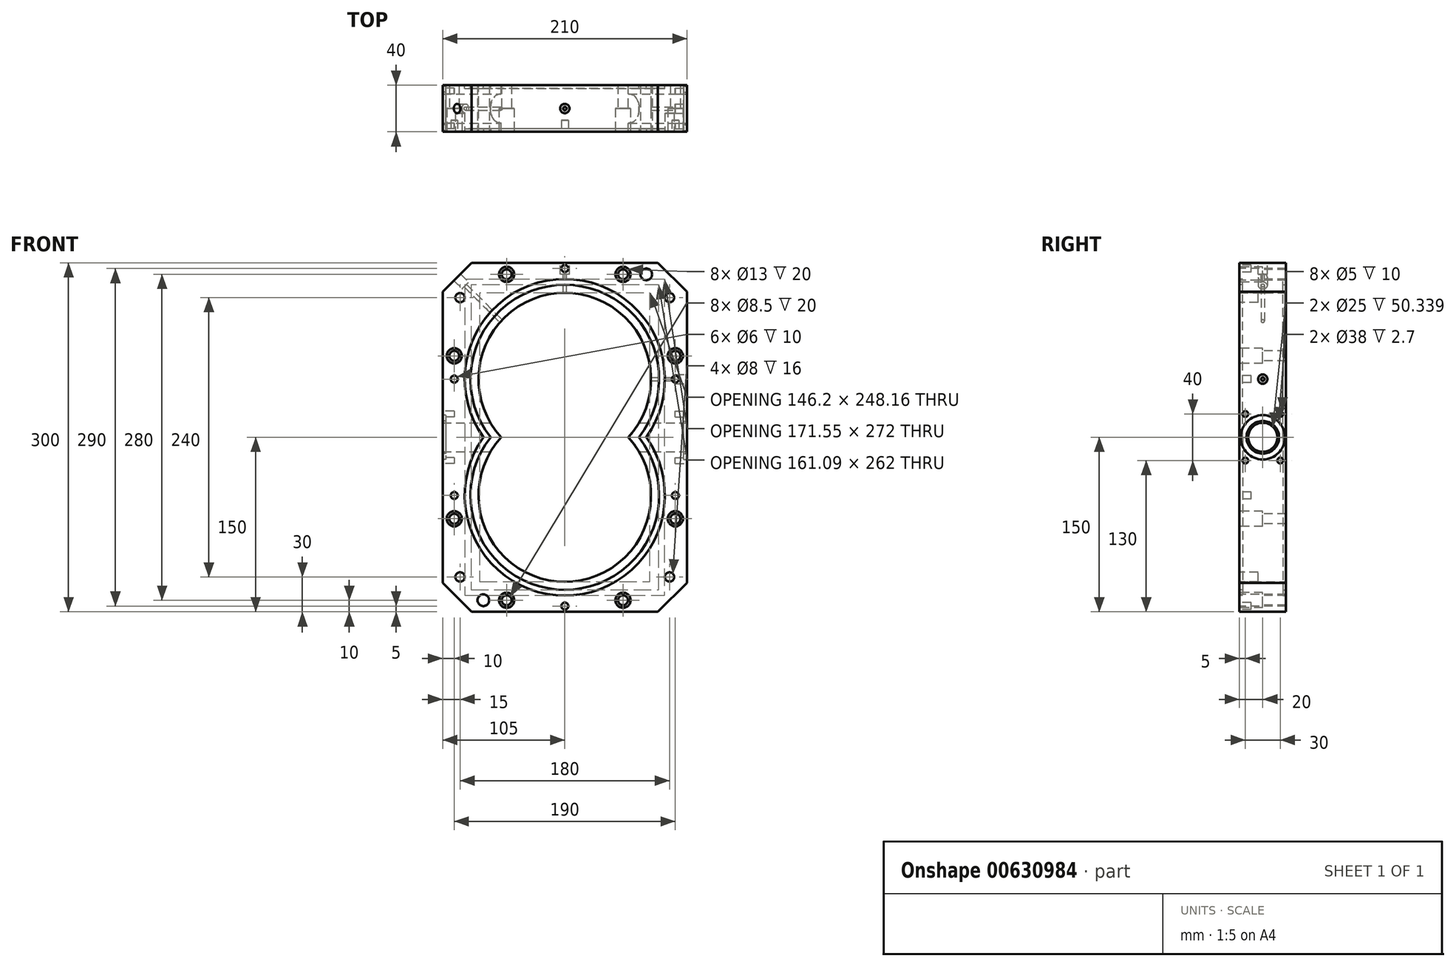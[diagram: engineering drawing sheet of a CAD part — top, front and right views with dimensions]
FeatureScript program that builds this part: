
annotation { "Feature Type Name" : "Feature", "Feature Type Description" : "" }
export const myFeature = defineFeature(function(context is Context, id is Id, definition is map)
    precondition{}
    {
        {
            var Q0;
            Q0=qCreatedBy(makeId("Front.planeOp"),FACE);
            var sketch = newSketch(context, id + "F0", { "sketchPlane" : qUnion([Q0])});
            skArc(sketch, "E0", {"start": v(54.66, 0) * mm, "mid": v(0, 124.08) * mm, "end": v(-54.66, 0) * mm});
            skArc(sketch, "E1", {"start": v(-54.66, 0) * mm, "mid": v(0, -124.08) * mm, "end": v(54.66, 0) * mm});
            skLineSegment(sketch, "E2.bottom", {"start": v(-80, 150) * mm, "end": v(80, 150) * mm});
            skLineSegment(sketch, "E2.top", {"start": v(-80, -150) * mm, "end": v(80, -150) * mm});
            skLineSegment(sketch, "E2.left", {"start": v(-105, 125) * mm, "end": v(-105, -125) * mm});
            skLineSegment(sketch, "E2.right", {"start": v(105, 125) * mm, "end": v(105, -125) * mm});
            skLineSegment(sketch, "E3", {"start": v(-80, 150) * mm, "end": v(-105, 125) * mm});
            skLineSegment(sketch, "E4", {"start": v(-105, -125) * mm, "end": v(-80, -150) * mm});
            skLineSegment(sketch, "E5", {"start": v(80, -150) * mm, "end": v(105, -125) * mm});
            skLineSegment(sketch, "E6", {"start": v(80, 150) * mm, "end": v(105, 125) * mm});
            skPoint(sketch, "E7.orphan", {"position": v(-105, 150) * mm});
            skSolve(sketch);
        }
        {
            var Q0;
            Q0=makeQuery(id+"F0.imprint","IMPRINT",FACE,{"disambiguationData":[TD([[makeQuery(id+"F0.imprint","IMPRINT",EDGE,{"derivedFrom":sQuery(id+"F0.wireOp",EDGE,"E0")}),-1.0]])]});
            extrude(context, id + "F1", {"entities" : qUnion([Q0]), "endBound" : BoundingType.SYMMETRIC, "depth" : 40 * mm, "offsetDistance" : 25 * mm});
        }
        {
            var Q0;
            Q0=makeQuery(id+"F1.opExtrude","SWEPT_FACE",FACE,{"disambiguationData":[OSD([sQuery(id+"F0.wireOp",EDGE,"E2.right")])]});
            var sketch = newSketch(context, id + "F2", { "sketchPlane" : qUnion([Q0])});
            skCircle(sketch, "E8", {"center": v(0, 0) * mm, "radius": 12.5 * mm});
            skSolve(sketch);
        }
        {
            var Q0;
            Q0=makeQuery(id+"F2.imprint","IMPRINT",FACE,{"disambiguationData":[TD([[makeQuery(id+"F2.imprint","IMPRINT",EDGE,{"derivedFrom":sQuery(id+"F2.wireOp",EDGE,"E8")}),1.0]])]});
            extrude(context, id + "F3", {"entities" : qUnion([Q0]), "operationType" : NewBodyOperationType.REMOVE, "endBound" : BoundingType.THROUGH_ALL, "oppositeDirection" : true, "depth" : 25 * mm, "offsetDistance" : 25 * mm});
        }
        {
            var Q0;
            Q0=makeQuery(id+"F1.opExtrude","SWEPT_FACE",FACE,{"disambiguationData":[OSD([sQuery(id+"F0.wireOp",EDGE,"E2.right")])]});
            var sketch = newSketch(context, id + "F4", { "sketchPlane" : qUnion([Q0])});
            skCircle(sketch, "E9", {"center": v(0, 0) * mm, "radius": 14 * mm});
            skCircle(sketch, "E10", {"center": v(0, 0) * mm, "radius": 19 * mm});
            skSolve(sketch);
        }
        {
            var Q0;
            Q0=makeQuery(id+"F4.imprint","IMPRINT",FACE,{"disambiguationData":[TD([[makeQuery(id+"F4.imprint","IMPRINT",EDGE,{"derivedFrom":sQuery(id+"F4.wireOp",EDGE,"E9")}),-1.0]])]});
            extrude(context, id + "F5", {"entities" : qUnion([Q0]), "operationType" : NewBodyOperationType.REMOVE, "oppositeDirection" : true, "depth" : 2.7 * mm, "offsetDistance" : 25 * mm});
        }
        {
            var Q0;
            Q0=makeQuery(id+"F1.opExtrude","SWEPT_FACE",FACE,{"disambiguationData":[OSD([sQuery(id+"F0.wireOp",EDGE,"E2.left")])]});
            var sketch = newSketch(context, id + "F6", { "sketchPlane" : qUnion([Q0])});
            skCircle(sketch, "E11", {"center": v(0, 0) * mm, "radius": 14 * mm});
            skCircle(sketch, "E12", {"center": v(0, 0) * mm, "radius": 19 * mm});
            skSolve(sketch);
        }
        {
            var Q0;
            Q0=makeQuery(id+"F6.imprint","IMPRINT",FACE,{"disambiguationData":[TD([[makeQuery(id+"F6.imprint","IMPRINT",EDGE,{"derivedFrom":sQuery(id+"F6.wireOp",EDGE,"E11")}),-1.0]])]});
            extrude(context, id + "F7", {"entities" : qUnion([Q0]), "operationType" : NewBodyOperationType.REMOVE, "oppositeDirection" : true, "depth" : 2.7 * mm, "offsetDistance" : 25 * mm});
        }
        {
            var Q0;
            Q0=makeQuery(id+"F1.opExtrude","CAP_FACE",FACE,{"disambiguationData":[OSD([sQuery(id+"F0.wireOp",EDGE,"E0"),sQuery(id+"F0.wireOp",EDGE,"E1"),sQuery(id+"F0.wireOp",EDGE,"E2.bottom"),sQuery(id+"F0.wireOp",EDGE,"E2.top"),sQuery(id+"F0.wireOp",EDGE,"E2.left"),sQuery(id+"F0.wireOp",EDGE,"E2.right"),sQuery(id+"F0.wireOp",EDGE,"E3"),sQuery(id+"F0.wireOp",EDGE,"E4"),sQuery(id+"F0.wireOp",EDGE,"E5"),sQuery(id+"F0.wireOp",EDGE,"E6")])],"isStart":true});
            var sketch = newSketch(context, id + "F8", { "sketchPlane" : qUnion([Q0])});
            skArc(sketch, "E13", {"start": v(63.73, 0) * mm, "mid": v(0, 131) * mm, "end": v(-63.73, 0) * mm});
            skArc(sketch, "E14", {"start": v(-63.73, 0) * mm, "mid": v(0, -131) * mm, "end": v(63.73, 0) * mm});
            skLineSegment(sketch, "E15", {"start": v(0, 131) * mm, "end": v(0, -131) * mm});
            skArc(sketch, "E16", {"start": v(69.97, 0) * mm, "mid": v(0, 136) * mm, "end": v(-69.97, 0) * mm});
            skArc(sketch, "E17", {"start": v(-69.97, 0) * mm, "mid": v(0, -136) * mm, "end": v(69.97, 0) * mm});
            skSolve(sketch);
        }
        {
            var Q0;
            Q0 = qSketchRegion(id + "F8", true);
            extrude(context, id + "F9", {"entities" : qUnion([Q0]), "operationType" : NewBodyOperationType.REMOVE, "oppositeDirection" : true, "depth" : 2.7 * mm, "offsetDistance" : 25 * mm});
        }
        {
            var Q0;
            Q0=makeQuery(id+"F1.opExtrude","CAP_FACE",FACE,{"disambiguationData":[OSD([sQuery(id+"F0.wireOp",EDGE,"E0"),sQuery(id+"F0.wireOp",EDGE,"E1"),sQuery(id+"F0.wireOp",EDGE,"E2.bottom"),sQuery(id+"F0.wireOp",EDGE,"E2.top"),sQuery(id+"F0.wireOp",EDGE,"E2.left"),sQuery(id+"F0.wireOp",EDGE,"E2.right"),sQuery(id+"F0.wireOp",EDGE,"E3"),sQuery(id+"F0.wireOp",EDGE,"E4"),sQuery(id+"F0.wireOp",EDGE,"E5"),sQuery(id+"F0.wireOp",EDGE,"E6")])],"isStart":false});
            var sketch = newSketch(context, id + "F10", { "sketchPlane" : qUnion([Q0])});
            skArc(sketch, "E18", {"start": v(63.73, 0) * mm, "mid": v(0, 131) * mm, "end": v(-63.73, 0) * mm});
            skArc(sketch, "E19", {"start": v(-63.73, 0) * mm, "mid": v(0, -131) * mm, "end": v(63.73, 0) * mm});
            skArc(sketch, "E20", {"start": v(-69.97, 0) * mm, "mid": v(0, -136) * mm, "end": v(69.97, 0) * mm});
            skArc(sketch, "E21", {"start": v(69.97, 0) * mm, "mid": v(0, 136) * mm, "end": v(-69.97, 0) * mm});
            skLineSegment(sketch, "E22", {"start": v(0, 131) * mm, "end": v(0, -131) * mm});
            skPoint(sketch, "E22.startSnap0", {"position": v(0, 124.08) * mm});
            skSolve(sketch);
        }
        {
            var Q0;
            Q0 = qSketchRegion(id + "F10", true);
            extrude(context, id + "F11", {"entities" : qUnion([Q0]), "operationType" : NewBodyOperationType.REMOVE, "oppositeDirection" : true, "depth" : 2.7 * mm, "offsetDistance" : 25 * mm});
        }
        {
            var Q0;
            {var subQ0=sQuery(id+"F0.wireOp",EDGE,"E5");var subQ4=sQuery(id+"F0.wireOp",EDGE,"E2.right");Q0=makeQuery(id+"F5.boolean.opBoolean","SPLIT",FACE,{"disambiguationData":[TD([makeQuery(id+"F1.opExtrude","SWEPT_FACE",FACE,{"disambiguationData":[OSD([subQ0])]})])],"derivedFrom":makeQuery(id+"F1.opExtrude","SWEPT_FACE",FACE,{"disambiguationData":[OSD([subQ4])]})});}
            var sketch = newSketch(context, id + "F12", { "sketchPlane" : qUnion([Q0])});
            skCircle(sketch, "E23", {"center": v(-15, 20) * mm, "radius": 2.5 * mm});
            skCircle(sketch, "E24", {"center": v(15, 20) * mm, "radius": 2.5 * mm});
            skCircle(sketch, "E25", {"center": v(15, -20) * mm, "radius": 2.5 * mm});
            skCircle(sketch, "E26", {"center": v(-15, -20) * mm, "radius": 2.5 * mm});
            skSolve(sketch);
        }
        {
            var Q0;
            Q0 = qSketchRegion(id + "F12", true);
            extrude(context, id + "F13", {"entities" : qUnion([Q0]), "operationType" : NewBodyOperationType.REMOVE, "oppositeDirection" : true, "depth" : 10 * mm, "offsetDistance" : 25 * mm});
        }
        {
            var Q0;
            {var subQ1=sQuery(id+"F0.wireOp",EDGE,"E3");var subQ5=sQuery(id+"F0.wireOp",EDGE,"E2.left");Q0=makeQuery(id+"F7.boolean.opBoolean","SPLIT",FACE,{"disambiguationData":[TD([makeQuery(id+"F1.opExtrude","SWEPT_FACE",FACE,{"disambiguationData":[OSD([subQ1])]})])],"derivedFrom":makeQuery(id+"F1.opExtrude","SWEPT_FACE",FACE,{"disambiguationData":[OSD([subQ5])]})});}
            var sketch = newSketch(context, id + "F14", { "sketchPlane" : qUnion([Q0])});
            skCircle(sketch, "E27", {"center": v(-15, 20) * mm, "radius": 2.5 * mm});
            skCircle(sketch, "E28", {"center": v(15, 20) * mm, "radius": 2.5 * mm});
            skCircle(sketch, "E29", {"center": v(15, -20) * mm, "radius": 2.5 * mm});
            skCircle(sketch, "E30", {"center": v(-15, -20) * mm, "radius": 2.5 * mm});
            skSolve(sketch);
        }
        {
            var Q0;
            Q0 = qSketchRegion(id + "F14", true);
            extrude(context, id + "F15", {"entities" : qUnion([Q0]), "operationType" : NewBodyOperationType.REMOVE, "oppositeDirection" : true, "depth" : 10 * mm, "offsetDistance" : 25 * mm});
        }
        {
            var Q0;
            {var subQ0=sQuery(id+"F0.wireOp",EDGE,"E2.right");var subQ1=sQuery(id+"F0.wireOp",EDGE,"E2.left");var subQ2=sQuery(id+"F0.wireOp",EDGE,"E2.top");var subQ3=sQuery(id+"F0.wireOp",EDGE,"E2.bottom");var subQ4=sQuery(id+"F0.wireOp",EDGE,"E3");var subQ5=sQuery(id+"F0.wireOp",EDGE,"E4");var subQ6=sQuery(id+"F0.wireOp",EDGE,"E5");var subQ7=sQuery(id+"F0.wireOp",EDGE,"E6");Q0=makeQuery(id+"F11.boolean.opBoolean","SPLIT",FACE,{"disambiguationData":[TD([makeQuery(id+"F1.opExtrude","SWEPT_FACE",FACE,{"disambiguationData":[OSD([subQ3])]})])],"derivedFrom":makeQuery(id+"F1.opExtrude","CAP_FACE",FACE,{"disambiguationData":[OSD([sQuery(id+"F0.wireOp",EDGE,"E0"),sQuery(id+"F0.wireOp",EDGE,"E1"),subQ3,subQ2,subQ1,subQ0,subQ4,subQ5,subQ6,subQ7])],"isStart":false})});}
            var sketch = newSketch(context, id + "F16", { "sketchPlane" : qUnion([Q0])});
            skCircle(sketch, "E31", {"center": v(-50, 140) * mm, "radius": 6.5 * mm});
            skCircle(sketch, "E32", {"center": v(50, 140) * mm, "radius": 6.5 * mm});
            skCircle(sketch, "E33", {"center": v(-50, -140) * mm, "radius": 6.5 * mm});
            skCircle(sketch, "E34", {"center": v(50, -140) * mm, "radius": 6.5 * mm});
            skCircle(sketch, "E35", {"center": v(95, 70) * mm, "radius": 6.5 * mm});
            skCircle(sketch, "E36", {"center": v(95, -70) * mm, "radius": 6.5 * mm});
            skCircle(sketch, "E37", {"center": v(-95, 70) * mm, "radius": 6.5 * mm});
            skCircle(sketch, "E38", {"center": v(-95, -70) * mm, "radius": 6.5 * mm});
            skSolve(sketch);
        }
        {
            var Q0;
            Q0 = qSketchRegion(id + "F16", true);
            extrude(context, id + "F17", {"entities" : qUnion([Q0]), "operationType" : NewBodyOperationType.REMOVE, "oppositeDirection" : true, "depth" : 20 * mm, "offsetDistance" : 25 * mm});
        }
        {
            var Q0;
            {var subQ0=sQuery(id+"F0.wireOp",EDGE,"E2.right");var subQ1=sQuery(id+"F0.wireOp",EDGE,"E2.left");var subQ2=sQuery(id+"F0.wireOp",EDGE,"E2.top");var subQ3=sQuery(id+"F0.wireOp",EDGE,"E2.bottom");var subQ4=sQuery(id+"F0.wireOp",EDGE,"E3");var subQ5=sQuery(id+"F0.wireOp",EDGE,"E4");var subQ6=sQuery(id+"F0.wireOp",EDGE,"E5");var subQ7=sQuery(id+"F0.wireOp",EDGE,"E6");Q0=makeQuery(id+"F11.boolean.opBoolean","SPLIT",FACE,{"disambiguationData":[TD([makeQuery(id+"F1.opExtrude","SWEPT_FACE",FACE,{"disambiguationData":[OSD([subQ3])]})])],"derivedFrom":makeQuery(id+"F1.opExtrude","CAP_FACE",FACE,{"disambiguationData":[OSD([sQuery(id+"F0.wireOp",EDGE,"E0"),sQuery(id+"F0.wireOp",EDGE,"E1"),subQ3,subQ2,subQ1,subQ0,subQ4,subQ5,subQ6,subQ7])],"isStart":false})});}
            var sketch = newSketch(context, id + "F18", { "sketchPlane" : qUnion([Q0])});
            skCircle(sketch, "E39", {"center": v(-50, 140) * mm, "radius": 4.25 * mm});
            skCircle(sketch, "E40", {"center": v(50, 140) * mm, "radius": 4.25 * mm});
            skCircle(sketch, "E41", {"center": v(95, 70) * mm, "radius": 4.25 * mm});
            skCircle(sketch, "E42", {"center": v(95, -70) * mm, "radius": 4.25 * mm});
            skCircle(sketch, "E43", {"center": v(50, -140) * mm, "radius": 4.25 * mm});
            skCircle(sketch, "E44", {"center": v(-50, -140) * mm, "radius": 4.25 * mm});
            skCircle(sketch, "E45", {"center": v(-95, -70) * mm, "radius": 4.25 * mm});
            skCircle(sketch, "E46", {"center": v(-95, 70) * mm, "radius": 4.25 * mm});
            skSolve(sketch);
        }
        {
            var Q0;
            Q0 = qSketchRegion(id + "F18", true);
            extrude(context, id + "F19", {"entities" : qUnion([Q0]), "operationType" : NewBodyOperationType.REMOVE, "endBound" : BoundingType.THROUGH_ALL, "oppositeDirection" : true, "depth" : 25 * mm, "offsetDistance" : 25 * mm});
        }
        {
            var Q0;
            {var subQ0=sQuery(id+"F0.wireOp",EDGE,"E2.right");var subQ1=sQuery(id+"F0.wireOp",EDGE,"E2.left");var subQ2=sQuery(id+"F0.wireOp",EDGE,"E2.top");var subQ3=sQuery(id+"F0.wireOp",EDGE,"E2.bottom");var subQ4=sQuery(id+"F0.wireOp",EDGE,"E3");var subQ5=sQuery(id+"F0.wireOp",EDGE,"E4");var subQ6=sQuery(id+"F0.wireOp",EDGE,"E5");var subQ7=sQuery(id+"F0.wireOp",EDGE,"E6");Q0=makeQuery(id+"F11.boolean.opBoolean","SPLIT",FACE,{"disambiguationData":[TD([makeQuery(id+"F1.opExtrude","SWEPT_FACE",FACE,{"disambiguationData":[OSD([subQ3])]})])],"derivedFrom":makeQuery(id+"F1.opExtrude","CAP_FACE",FACE,{"disambiguationData":[OSD([sQuery(id+"F0.wireOp",EDGE,"E0"),sQuery(id+"F0.wireOp",EDGE,"E1"),subQ3,subQ2,subQ1,subQ0,subQ4,subQ5,subQ6,subQ7])],"isStart":false})});}
            var sketch = newSketch(context, id + "F20", { "sketchPlane" : qUnion([Q0])});
            skCircle(sketch, "E47", {"center": v(0, 145) * mm, "radius": 3 * mm});
            skPoint(sketch, "E47.centerSnap0", {"position": v(0, 150) * mm});
            skPoint(sketch, "E48.centerSnap0", {"position": v(0, -136) * mm});
            skCircle(sketch, "E49", {"center": v(-95, 50) * mm, "radius": 3 * mm});
            skCircle(sketch, "E50", {"center": v(-95, -50) * mm, "radius": 3 * mm});
            skCircle(sketch, "E51", {"center": v(95, -50) * mm, "radius": 3 * mm});
            skCircle(sketch, "E52", {"center": v(95, 50) * mm, "radius": 3 * mm});
            skCircle(sketch, "E53", {"center": v(0, -145) * mm, "radius": 3 * mm});
            skSolve(sketch);
        }
        {
            var Q0;
            Q0 = qSketchRegion(id + "F20", true);
            extrude(context, id + "F21", {"entities" : qUnion([Q0]), "operationType" : NewBodyOperationType.REMOVE, "oppositeDirection" : true, "depth" : 10 * mm, "offsetDistance" : 25 * mm});
        }
        {
            var Q0;
            Q0=qCreatedBy(makeId("Front.planeOp"),FACE);
            var sketch = newSketch(context, id + "F22", { "sketchPlane" : qUnion([Q0])});
            skLineSegment(sketch, "E54", {"start": v(-92.5, 137.5) * mm, "end": v(0, 45) * mm});
            skLineSegment(sketch, "E55", {"start": v(-92.5, 137.5) * mm, "end": v(-89.67, 140.33) * mm});
            skLineSegment(sketch, "E56", {"start": v(-89.67, 140.33) * mm, "end": v(-82.6, 133.26) * mm});
            skLineSegment(sketch, "E57", {"start": v(-82.6, 133.26) * mm, "end": v(-85.43, 130.43) * mm});
            skLineSegment(sketch, "E58", {"start": v(-85.43, 130.43) * mm, "end": v(-49.19, 94.18) * mm});
            skLineSegment(sketch, "E59", {"start": v(-49.19, 94.18) * mm, "end": v(-48.13, 95.25) * mm});
            skLineSegment(sketch, "E60", {"start": v(-48.13, 95.25) * mm, "end": v(-84.37, 131.49) * mm});
            skSolve(sketch);
        }
        {
            var Q0;
            Q0 = qSketchRegion(id + "F22", true);
            var Q1;
            Q1=sQuery(id+"F22.wireOp",EDGE,"E54");
            revolve(context, id + "F23", {"operationType" : NewBodyOperationType.REMOVE, "entities" : qUnion([Q0]), "axis" : qUnion([Q1]), "revolveType" : RevolveType.FULL, "oppositeDirection" : true});
        }
        {
            var Q0;
            Q0=qCreatedBy(makeId("Front.planeOp"),FACE);
            var sketch = newSketch(context, id + "F24", { "sketchPlane" : qUnion([Q0])});
            skLineSegment(sketch, "E61", {"start": v(0, 0) * mm, "end": v(0, 162.66) * mm});
            skLineSegment(sketch, "E62.bottom", {"start": v(0, 162.66) * mm, "end": v(4, 162.66) * mm});
            skLineSegment(sketch, "E62.top", {"start": v(0, 140) * mm, "end": v(4, 140) * mm});
            skLineSegment(sketch, "E62.left", {"start": v(0, 162.66) * mm, "end": v(0, 140) * mm});
            skLineSegment(sketch, "E62.right", {"start": v(4, 162.66) * mm, "end": v(4, 140) * mm});
            skLineSegment(sketch, "E63.bottom", {"start": v(0, 140) * mm, "end": v(1.5, 140) * mm});
            skLineSegment(sketch, "E63.top", {"start": v(0, 111.94) * mm, "end": v(1.5, 111.94) * mm});
            skLineSegment(sketch, "E63.left", {"start": v(0, 140) * mm, "end": v(0, 111.94) * mm});
            skLineSegment(sketch, "E63.right", {"start": v(1.5, 140) * mm, "end": v(1.5, 111.94) * mm});
            skSolve(sketch);
        }
        {
            var Q0;
            Q0 = qSketchRegion(id + "F24", true);
            var Q1;
            Q1=sQuery(id+"F24.wireOp",EDGE,"E61");
            revolve(context, id + "F25", {"operationType" : NewBodyOperationType.REMOVE, "entities" : qUnion([Q0]), "axis" : qUnion([Q1]), "revolveType" : RevolveType.FULL, "oppositeDirection" : true});
        }
        {
            var Q0;
            Q0=qCreatedBy(makeId("Front.planeOp"),FACE);
            var sketch = newSketch(context, id + "F26", { "sketchPlane" : qUnion([Q0])});
            skLineSegment(sketch, "E64", {"start": v(-182.48, 50) * mm, "end": v(200.78, 50) * mm});
            skLineSegment(sketch, "E65.bottom", {"start": v(111.55, 50) * mm, "end": v(95, 50) * mm});
            skLineSegment(sketch, "E65.top", {"start": v(111.55, 46) * mm, "end": v(95, 46) * mm});
            skLineSegment(sketch, "E65.left", {"start": v(111.55, 50) * mm, "end": v(111.55, 46) * mm});
            skLineSegment(sketch, "E65.right", {"start": v(95, 50) * mm, "end": v(95, 46) * mm});
            skLineSegment(sketch, "E66.bottom", {"start": v(70.84, 50) * mm, "end": v(95, 50) * mm});
            skLineSegment(sketch, "E66.top", {"start": v(70.84, 48.5) * mm, "end": v(95, 48.5) * mm});
            skLineSegment(sketch, "E66.left", {"start": v(70.84, 50) * mm, "end": v(70.84, 48.5) * mm});
            skLineSegment(sketch, "E66.right", {"start": v(95, 50) * mm, "end": v(95, 48.5) * mm});
            skSolve(sketch);
        }
        {
            var Q0;
            Q0 = qSketchRegion(id + "F26", true);
            var Q1;
            Q1=sQuery(id+"F26.wireOp",EDGE,"E64");
            revolve(context, id + "F27", {"operationType" : NewBodyOperationType.REMOVE, "entities" : qUnion([Q0]), "axis" : qUnion([Q1]), "revolveType" : RevolveType.FULL, "oppositeDirection" : true});
        }
        {
            var Q0;
            {var subQ0=sQuery(id+"F0.wireOp",EDGE,"E2.right");var subQ1=sQuery(id+"F0.wireOp",EDGE,"E2.left");var subQ2=sQuery(id+"F0.wireOp",EDGE,"E2.top");var subQ3=sQuery(id+"F0.wireOp",EDGE,"E2.bottom");var subQ4=sQuery(id+"F0.wireOp",EDGE,"E3");var subQ5=sQuery(id+"F0.wireOp",EDGE,"E4");var subQ6=sQuery(id+"F0.wireOp",EDGE,"E5");var subQ7=sQuery(id+"F0.wireOp",EDGE,"E6");Q0=makeQuery(id+"F11.boolean.opBoolean","SPLIT",FACE,{"disambiguationData":[TD([makeQuery(id+"F1.opExtrude","SWEPT_FACE",FACE,{"disambiguationData":[OSD([subQ3])]})])],"derivedFrom":makeQuery(id+"F1.opExtrude","CAP_FACE",FACE,{"disambiguationData":[OSD([sQuery(id+"F0.wireOp",EDGE,"E0"),sQuery(id+"F0.wireOp",EDGE,"E1"),subQ3,subQ2,subQ1,subQ0,subQ4,subQ5,subQ6,subQ7])],"isStart":false})});}
            var sketch = newSketch(context, id + "F28", { "sketchPlane" : qUnion([Q0])});
            skCircle(sketch, "E67", {"center": v(70, 140) * mm, "radius": 5 * mm});
            skCircle(sketch, "E68", {"center": v(-70, -140) * mm, "radius": 5 * mm});
            skSolve(sketch);
        }
        {
            var Q0;
            Q0 = qSketchRegion(id + "F28", true);
            extrude(context, id + "F29", {"entities" : qUnion([Q0]), "operationType" : NewBodyOperationType.REMOVE, "endBound" : BoundingType.THROUGH_ALL, "oppositeDirection" : true, "depth" : 25 * mm, "offsetDistance" : 25 * mm});
        }
        {
            var Q0;
            {var subQ0=sQuery(id+"F0.wireOp",EDGE,"E2.right");var subQ1=sQuery(id+"F0.wireOp",EDGE,"E2.left");var subQ2=sQuery(id+"F0.wireOp",EDGE,"E2.top");var subQ3=sQuery(id+"F0.wireOp",EDGE,"E2.bottom");var subQ4=sQuery(id+"F0.wireOp",EDGE,"E3");var subQ5=sQuery(id+"F0.wireOp",EDGE,"E4");var subQ6=sQuery(id+"F0.wireOp",EDGE,"E5");var subQ7=sQuery(id+"F0.wireOp",EDGE,"E6");Q0=makeQuery(id+"F11.boolean.opBoolean","SPLIT",FACE,{"disambiguationData":[TD([makeQuery(id+"F1.opExtrude","SWEPT_FACE",FACE,{"disambiguationData":[OSD([subQ3])]})])],"derivedFrom":makeQuery(id+"F1.opExtrude","CAP_FACE",FACE,{"disambiguationData":[OSD([sQuery(id+"F0.wireOp",EDGE,"E0"),sQuery(id+"F0.wireOp",EDGE,"E1"),subQ3,subQ2,subQ1,subQ0,subQ4,subQ5,subQ6,subQ7])],"isStart":false})});}
            var sketch = newSketch(context, id + "F30", { "sketchPlane" : qUnion([Q0])});
            skCircle(sketch, "E69", {"center": v(-90, 120) * mm, "radius": 4 * mm});
            skCircle(sketch, "E70", {"center": v(90, 120) * mm, "radius": 4 * mm});
            skCircle(sketch, "E71", {"center": v(90, -120) * mm, "radius": 4 * mm});
            skCircle(sketch, "E72", {"center": v(-90, -120) * mm, "radius": 4 * mm});
            skSolve(sketch);
        }
        {
            var Q0;
            Q0 = qSketchRegion(id + "F30", true);
            extrude(context, id + "F31", {"entities" : qUnion([Q0]), "operationType" : NewBodyOperationType.REMOVE, "oppositeDirection" : true, "depth" : 16 * mm, "offsetDistance" : 25 * mm});
        }
    });
